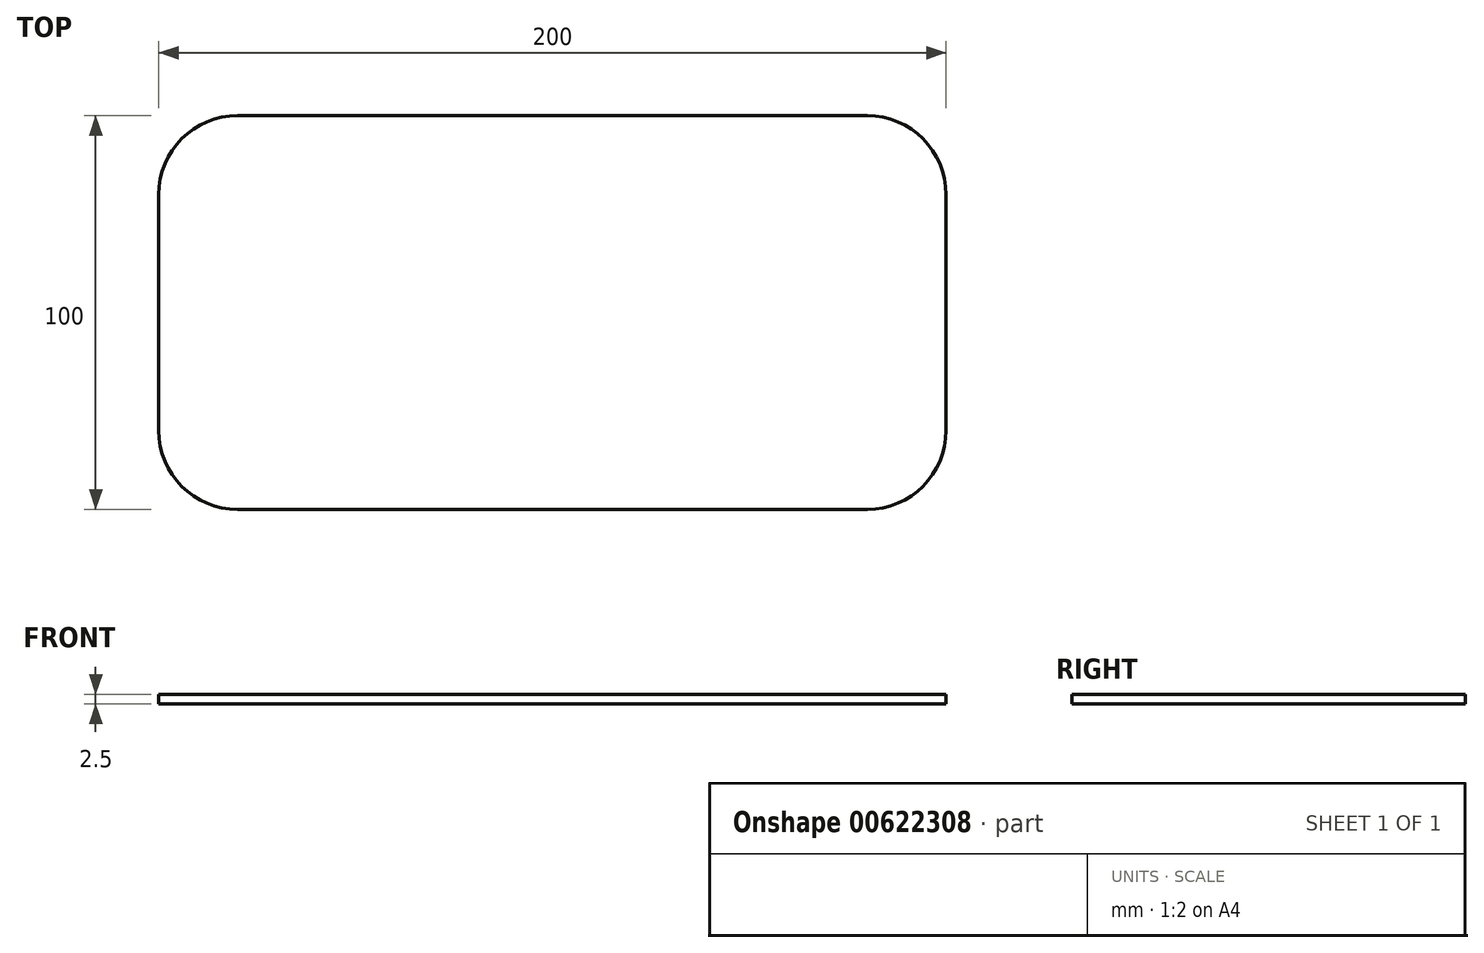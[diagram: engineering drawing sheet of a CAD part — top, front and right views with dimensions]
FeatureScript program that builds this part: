
annotation { "Feature Type Name" : "Feature", "Feature Type Description" : "" }
export const myFeature = defineFeature(function(context is Context, id is Id, definition is map)
    precondition{}
    {
        {
            assignVariable(context, id + "F0", {"name" : "d", "anyValue" : 2.5});
        }
        {
            var Q0;
            Q0=qCreatedBy(makeId("Top.planeOp"),FACE);
            var sketch = newSketch(context, id + "F1", { "sketchPlane" : qUnion([Q0])});
            skLineSegment(sketch, "E0.bottom", {"start": v(80, 50) * mm, "end": v(-80, 50) * mm});
            skLineSegment(sketch, "E0.top", {"start": v(80, -50) * mm, "end": v(-80, -50) * mm});
            skLineSegment(sketch, "E0.left", {"start": v(100, 30) * mm, "end": v(100, -30) * mm});
            skLineSegment(sketch, "E0.right", {"start": v(-100, 30) * mm, "end": v(-100, -30) * mm});
            skPoint(sketch, "E0.middle", {"position": v(0, 0) * mm});
            skPoint(sketch, "E1.visualSharp", {"position": v(100, 50) * mm});
            skArc(sketch, "E1.filletArc", {"start": v(100, 30) * mm, "mid": v(94.14, 44.14) * mm, "end": v(80, 50) * mm});
            skPoint(sketch, "E2.visualSharp", {"position": v(-100, 50) * mm});
            skArc(sketch, "E2.filletArc", {"start": v(-80, 50) * mm, "mid": v(-94.14, 44.14) * mm, "end": v(-100, 30) * mm});
            skPoint(sketch, "E3.visualSharp", {"position": v(-100, -50) * mm});
            skArc(sketch, "E3.filletArc", {"start": v(-100, -30) * mm, "mid": v(-94.14, -44.14) * mm, "end": v(-80, -50) * mm});
            skPoint(sketch, "E4.visualSharp", {"position": v(100, -50) * mm});
            skArc(sketch, "E4.filletArc", {"start": v(80, -50) * mm, "mid": v(94.14, -44.14) * mm, "end": v(100, -30) * mm});
            skSolve(sketch);
        }
        {
            var Q0;
            Q0=makeQuery(id+"F1.imprint","IMPRINT",FACE,{"disambiguationData":[TD([[makeQuery(id+"F1.imprint","IMPRINT",EDGE,{"derivedFrom":sQuery(id+"F1.wireOp",EDGE,"E0.bottom")}),1.0]])]});
            extrude(context, id + "F2", {"entities" : qUnion([Q0]), "depth" : (getVariable(context, 'd')) * mm, "offsetDistance" : 25 * mm});
        }
    });
